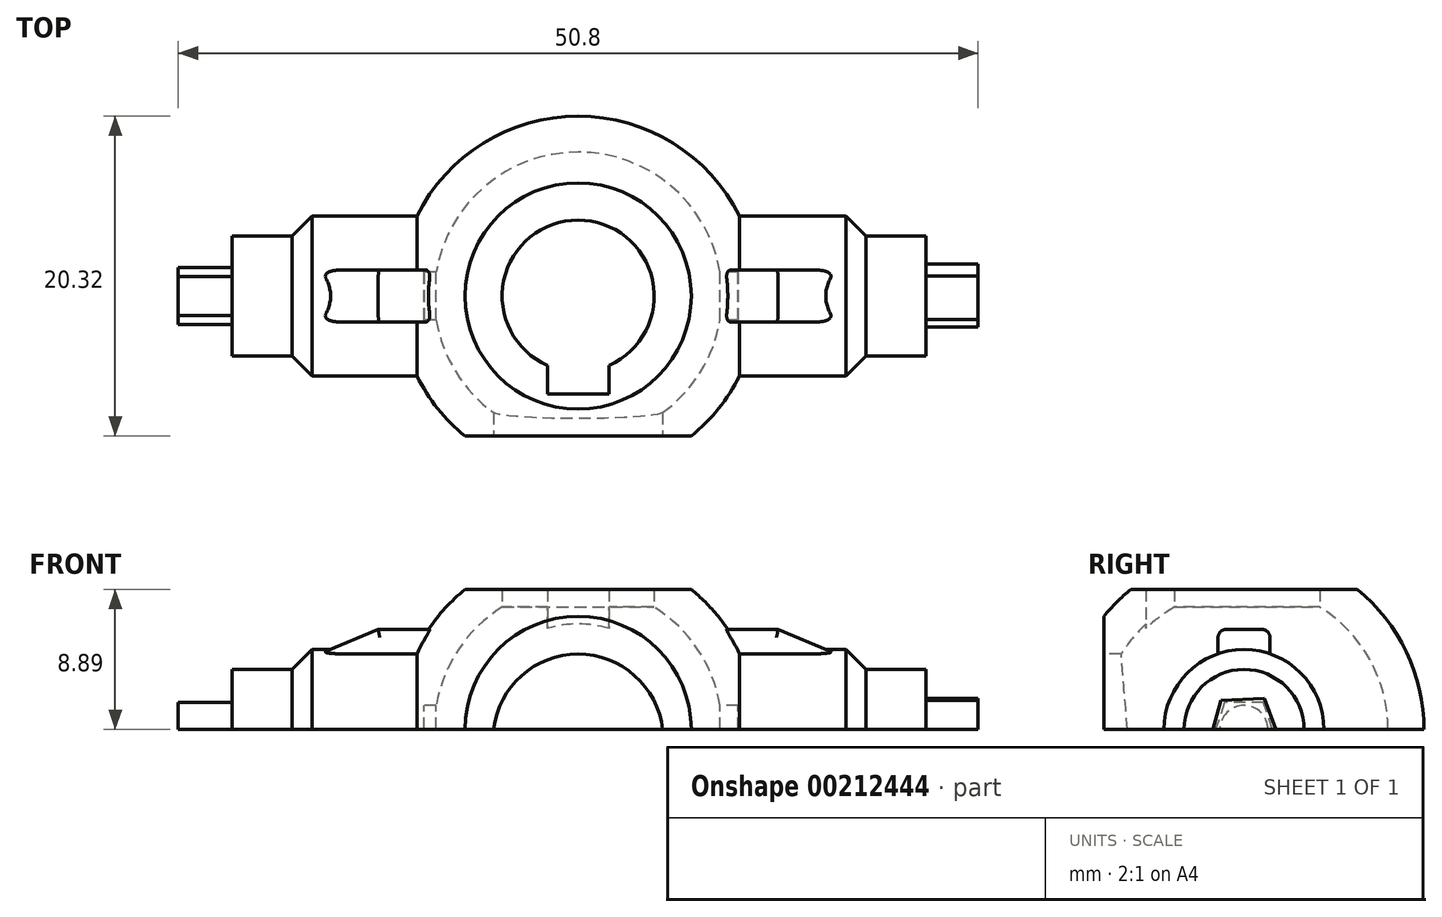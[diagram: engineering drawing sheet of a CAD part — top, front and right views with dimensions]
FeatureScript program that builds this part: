
annotation { "Feature Type Name" : "Feature", "Feature Type Description" : "" }
export const myFeature = defineFeature(function(context is Context, id is Id, definition is map)
    precondition{}
    {
        {
            var Q0;
            Q0=qCreatedBy(makeId("Top.planeOp"),FACE);
            var sketch = newSketch(context, id + "F0", { "sketchPlane" : qUnion([Q0])});
            skCircle(sketch, "E0", {"center": v(0, 0) * mm, "radius": 11.43 * mm});
            skSolve(sketch);
        }
        {
            var Q0;
            Q0=qCreatedBy(makeId("Right.planeOp"),FACE);
            var sketch = newSketch(context, id + "F1", { "sketchPlane" : qUnion([Q0])});
            skCircle(sketch, "E1", {"center": v(0, 0) * mm, "radius": 3.81 * mm});
            skSolve(sketch);
        }
        {
            var Q0;
            Q0=makeQuery(id+"F0.imprint","IMPRINT",FACE,{"disambiguationData":[TD([[makeQuery(id+"F0.imprint","IMPRINT",EDGE,{"derivedFrom":sQuery(id+"F0.wireOp",EDGE,"E0")}),1.0]])]});
            extrude(context, id + "F2", {"entities" : qUnion([Q0]), "depth" : 11.43 * mm});
        }
        {
            var Q0;
            Q0 = qSketchRegion(id + "F1", true);
            extrude(context, id + "F3", {"entities" : qUnion([Q0]), "operationType" : NewBodyOperationType.ADD, "depth" : 25.4 * mm, "hasSecondDirection" : true, "secondDirectionOppositeDirection" : true, "secondDirectionDepth" : 25.4 * mm});
        }
        {
            var Q0;
            Q0=makeQuery(id+"F2.opExtrude","CAP_EDGE",EDGE,{"disambiguationData":[OSD([sQuery(id+"F0.wireOp",EDGE,"E0")])],"isStart":false});
            fillet(context, id + "F4", {"entities" : qUnion([Q0]), "radius" : 11.43 * mm, "tangentPropagation" : true, "allowEdgeOverflow" : false});
        }
        {
            var Q0;
            Q0=makeQuery(id+"F2.opExtrude","CAP_FACE",FACE,{"disambiguationData":[OSD([sQuery(id+"F0.wireOp",EDGE,"E0")])],"isStart":true});
            shell(context, id + "F5", {"entities" : qUnion([Q0]), "thickness" : 2.3 * mm});
        }
        {
            var Q0;
            Q0=qCreatedBy(makeId("Top.planeOp"),FACE);
            var sketch = newSketch(context, id + "F6", { "sketchPlane" : qUnion([Q0])});
            skArc(sketch, "E2", {"start": v(1.96, -4.41) * mm, "mid": v(0, 4.83) * mm, "end": v(-1.94, -4.42) * mm});
            skLineSegment(sketch, "E3", {"start": v(0, -6.22) * mm, "end": v(-1.94, -6.22) * mm});
            skLineSegment(sketch, "E4", {"start": v(-1.94, -6.22) * mm, "end": v(-1.94, -4.42) * mm});
            skLineSegment(sketch, "E5", {"start": v(0, -6.22) * mm, "end": v(1.96, -6.22) * mm});
            skLineSegment(sketch, "E6", {"start": v(1.96, -6.22) * mm, "end": v(1.96, -4.41) * mm});
            skPoint(sketch, "E7.orphan", {"position": v(-1.94, 0) * mm});
            skPoint(sketch, "E8.orphan", {"position": v(1.96, 0) * mm});
            skSolve(sketch);
        }
        {
            var Q0;
            Q0 = qSketchRegion(id + "F6", true);
            extrude(context, id + "F7", {"entities" : qUnion([Q0]), "operationType" : NewBodyOperationType.REMOVE, "depth" : 25.4 * mm});
        }
        {
            var Q0;
            Q0=qCreatedBy(makeId("Top.planeOp"),FACE);
            var sketch = newSketch(context, id + "F8", { "sketchPlane" : qUnion([Q0])});
            skCircle(sketch, "E9", {"center": v(0, 0) * mm, "radius": 9.15 * mm});
            skSolve(sketch);
        }
        {
            var Q0;
            Q0 = qSketchRegion(id + "F8", true);
            extrude(context, id + "F9", {"entities" : qUnion([Q0]), "operationType" : NewBodyOperationType.REMOVE, "oppositeDirection" : true, "depth" : 25.4 * mm});
        }
        {
            var Q0;
            Q0=makeQuery(id+"F3.opExtrude","CAP_FACE",FACE,{"disambiguationData":[OSD([sQuery(id+"F1.wireOp",EDGE,"E1")])],"isStart":false});
            var sketch = newSketch(context, id + "F10", { "sketchPlane" : qUnion([Q0])});
            skCircle(sketch, "E10.cCircle", {"center": v(0, 0) * mm, "radius": 1.9 * mm, "construction": true});
            skLineSegment(sketch, "E10.0", {"start": v(1.28, 1.97) * mm, "end": v(2.27, -0.6) * mm});
            skLineSegment(sketch, "E10.1", {"start": v(2.27, -0.6) * mm, "end": v(0.12, -2.35) * mm});
            skLineSegment(sketch, "E10.2", {"start": v(0.12, -2.35) * mm, "end": v(-2.2, -0.84) * mm});
            skLineSegment(sketch, "E10.3", {"start": v(-2.2, -0.84) * mm, "end": v(-1.48, 1.83) * mm});
            skLineSegment(sketch, "E10.4", {"start": v(-1.48, 1.83) * mm, "end": v(1.28, 1.97) * mm});
            skPoint(sketch, "E10.0.midPoint", {"position": v(1.78, 0.68) * mm});
            skCircle(sketch, "E11", {"center": v(0, 0) * mm, "radius": 3.82 * mm});
            skSolve(sketch);
        }
        {
            var Q0;
            Q0 = qSketchRegion(id + "F10", true);
            extrude(context, id + "F11", {"entities" : qUnion([Q0]), "operationType" : NewBodyOperationType.REMOVE, "oppositeDirection" : true, "depth" : 3.3 * mm});
        }
        {
            var Q0;
            Q0=makeQuery(id+"F3.opExtrude","CAP_FACE",FACE,{"disambiguationData":[OSD([sQuery(id+"F1.wireOp",EDGE,"E1")])],"isStart":true});
            var sketch = newSketch(context, id + "F12", { "sketchPlane" : qUnion([Q0])});
            skCircle(sketch, "E12.cCircle", {"center": v(0, 0) * mm, "radius": 1.71 * mm, "construction": true});
            skLineSegment(sketch, "E12.0", {"start": v(-1.25, 1.71) * mm, "end": v(1.25, 1.71) * mm});
            skLineSegment(sketch, "E12.1", {"start": v(1.25, 1.71) * mm, "end": v(2.02, -0.65) * mm});
            skLineSegment(sketch, "E12.2", {"start": v(2.02, -0.65) * mm, "end": v(0, -2.12) * mm});
            skLineSegment(sketch, "E12.3", {"start": v(0, -2.12) * mm, "end": v(-2.02, -0.65) * mm});
            skLineSegment(sketch, "E12.4", {"start": v(-2.02, -0.65) * mm, "end": v(-1.25, 1.71) * mm});
            skPoint(sketch, "E12.0.midPoint", {"position": v(0, 1.71) * mm});
            skCircle(sketch, "E13", {"center": v(0, 0) * mm, "radius": 3.96 * mm});
            skSolve(sketch);
        }
        {
            var Q0;
            Q0 = qSketchRegion(id + "F12", true);
            extrude(context, id + "F13", {"entities" : qUnion([Q0]), "operationType" : NewBodyOperationType.REMOVE, "oppositeDirection" : true, "depth" : 3.43 * mm});
        }
        {
            var Q0;
            Q0=qCreatedBy(makeId("Right.planeOp"),FACE);
            var sketch = newSketch(context, id + "F14", { "sketchPlane" : qUnion([Q0])});
            skLineSegment(sketch, "E14", {"start": v(0, 0) * mm, "end": v(4.49, 0) * mm});
            skLineSegment(sketch, "E15", {"start": v(4.49, 0) * mm, "end": v(4.49, -5.61) * mm});
            skLineSegment(sketch, "E16", {"start": v(4.49, -5.61) * mm, "end": v(-4.03, -5.61) * mm});
            skLineSegment(sketch, "E17", {"start": v(-4.03, -5.61) * mm, "end": v(-4.03, 0) * mm});
            skLineSegment(sketch, "E18", {"start": v(-4.03, 0) * mm, "end": v(0, 0) * mm});
            skSolve(sketch);
        }
        {
            var Q0;
            Q0 = qSketchRegion(id + "F14", true);
            extrude(context, id + "F15", {"entities" : qUnion([Q0]), "operationType" : NewBodyOperationType.REMOVE, "endBound" : BoundingType.THROUGH_ALL, "oppositeDirection" : true, "depth" : 25.4 * mm, "hasSecondDirection" : true, "secondDirectionBound" : SecondDirectionBoundingType.THROUGH_ALL, "secondDirectionOppositeDirection" : false, "secondDirectionDepth" : 25.4 * mm});
        }
        {
            var Q0;
            {var subQ0=sQuery(id+"F1.wireOp",EDGE,"E1");Q0=makeQuery(id+"F5.opShell","OFFSET_FACE",FACE,{"disambiguationData":[OSD([subQ0]),TDD([makeQuery(id+"F3.opExtrude","CAP_FACE",FACE,{"disambiguationData":[OSD([subQ0])],"isStart":false})])]});}
            var sketch = newSketch(context, id + "F16", { "sketchPlane" : qUnion([Q0])});
            skLineSegment(sketch, "E19", {"start": v(-1.52, 0) * mm, "end": v(1.52, 0) * mm});
            skArc(sketch, "E20", {"start": v(1.52, 0) * mm, "mid": v(0, 1.53) * mm, "end": v(-1.52, 0) * mm});
            skSolve(sketch);
        }
        {
            var Q0;
            Q0 = qSketchRegion(id + "F16", true);
            extrude(context, id + "F17", {"entities" : qUnion([Q0]), "operationType" : NewBodyOperationType.ADD, "depth" : 7.62 * mm});
        }
        {
            var Q0;
            {var subQ0=sQuery(id+"F1.wireOp",EDGE,"E1");Q0=makeQuery(id+"F5.opShell","OFFSET_FACE",FACE,{"disambiguationData":[OSD([subQ0]),TDD([makeQuery(id+"F3.opExtrude","CAP_FACE",FACE,{"disambiguationData":[OSD([subQ0])],"isStart":true})])]});}
            var sketch = newSketch(context, id + "F18", { "sketchPlane" : qUnion([Q0])});
            skLineSegment(sketch, "E21", {"start": v(1.52, 0) * mm, "end": v(-1.52, 0) * mm});
            skArc(sketch, "E22", {"start": v(1.52, 0) * mm, "mid": v(0, 1.58) * mm, "end": v(-1.52, 0) * mm});
            skSolve(sketch);
        }
        {
            var Q0;
            Q0 = qSketchRegion(id + "F18", true);
            extrude(context, id + "F19", {"entities" : qUnion([Q0]), "operationType" : NewBodyOperationType.ADD, "depth" : 7.62 * mm});
        }
        {
            var Q0;
            Q0=qCreatedBy(makeId("Front.planeOp"),FACE);
            var sketch = newSketch(context, id + "F20", { "sketchPlane" : qUnion([Q0])});
            skLineSegment(sketch, "E23", {"start": v(7.45, 6.35) * mm, "end": v(12.7, 6.35) * mm});
            skLineSegment(sketch, "E24", {"start": v(-7.45, 6.35) * mm, "end": v(-12.7, 6.35) * mm});
            skArc(sketch, "E25", {"start": v(9.07, 3.68) * mm, "mid": v(8.37, 5.08) * mm, "end": v(7.45, 6.35) * mm});
            skLineSegment(sketch, "E26", {"start": v(12.7, 6.35) * mm, "end": v(19.05, 3.68) * mm});
            skLineSegment(sketch, "E27", {"start": v(-12.7, 6.35) * mm, "end": v(-19.05, 3.68) * mm});
            skArc(sketch, "E28.trimOffspring", {"start": v(-7.45, 6.35) * mm, "mid": v(-8.37, 5.08) * mm, "end": v(-9.07, 3.68) * mm});
            skLineSegment(sketch, "E29", {"start": v(-19.05, 2.55) * mm, "end": v(-9.07, 2.55) * mm});
            skLineSegment(sketch, "E30", {"start": v(19.05, 2.55) * mm, "end": v(19.05, 3.68) * mm});
            skLineSegment(sketch, "E31", {"start": v(-19.05, 3.68) * mm, "end": v(-19.05, 2.55) * mm});
            skLineSegment(sketch, "E32", {"start": v(-9.07, 3.68) * mm, "end": v(-9.07, 2.55) * mm});
            skLineSegment(sketch, "E33", {"start": v(9.07, 3.68) * mm, "end": v(9.07, 2.55) * mm});
            skLineSegment(sketch, "E34.trimOffspring", {"start": v(9.07, 2.55) * mm, "end": v(19.05, 2.55) * mm});
            skSolve(sketch);
        }
        {
            var Q0;
            Q0 = qSketchRegion(id + "F20", true);
            extrude(context, id + "F21", {"entities" : qUnion([Q0]), "operationType" : NewBodyOperationType.ADD, "depth" : 1.65 * mm, "hasSecondDirection" : true, "secondDirectionOppositeDirection" : true, "secondDirectionDepth" : 1.65 * mm});
        }
        {
            var Q0;
            Q0=makeQuery(id+"F21.opExtrude","CAP_EDGE",EDGE,{"disambiguationData":[OSD([sQuery(id+"F20.wireOp",EDGE,"E23")])],"isStart":false});
            var Q1;
            Q1=makeQuery(id+"F21.opExtrude","CAP_EDGE",EDGE,{"disambiguationData":[OSD([sQuery(id+"F20.wireOp",EDGE,"E23")])],"isStart":true});
            var Q2;
            Q2=makeQuery(id+"F21.opExtrude","CAP_EDGE",EDGE,{"disambiguationData":[OSD([sQuery(id+"F20.wireOp",EDGE,"E24")])],"isStart":false});
            var Q3;
            Q3=makeQuery(id+"F21.opExtrude","CAP_EDGE",EDGE,{"disambiguationData":[OSD([sQuery(id+"F20.wireOp",EDGE,"E24")])],"isStart":true});
            var Q4;
            Q4=makeQuery(id+"F21.opExtrude","CAP_EDGE",EDGE,{"disambiguationData":[OSD([sQuery(id+"F20.wireOp",EDGE,"E27")])],"isStart":true});
            var Q5;
            Q5=makeQuery(id+"F21.opExtrude","CAP_EDGE",EDGE,{"disambiguationData":[OSD([sQuery(id+"F20.wireOp",EDGE,"E27")])],"isStart":false});
            var Q6;
            Q6=makeQuery(id+"F21.opExtrude","CAP_EDGE",EDGE,{"disambiguationData":[OSD([sQuery(id+"F20.wireOp",EDGE,"E26")])],"isStart":false});
            var Q7;
            Q7=makeQuery(id+"F21.opExtrude","CAP_EDGE",EDGE,{"disambiguationData":[OSD([sQuery(id+"F20.wireOp",EDGE,"E26")])],"isStart":true});
            fillet(context, id + "F22", {"entities" : qUnion([Q0, Q1, Q2, Q3, Q4, Q5, Q6, Q7]), "radius" : 0.5 * mm, "tangentPropagation" : true, "allowEdgeOverflow" : false});
        }
        {
            var Q0;
            Q0=qCreatedBy(makeId("Right.planeOp"),FACE);
            var sketch = newSketch(context, id + "F23", { "sketchPlane" : qUnion([Q0])});
            skLineSegment(sketch, "E35", {"start": v(12.7, 8.9) * mm, "end": v(-12.7, 8.89) * mm});
            skLineSegment(sketch, "E36", {"start": v(12.7, 8.9) * mm, "end": v(12.7, 12.27) * mm});
            skLineSegment(sketch, "E37", {"start": v(12.7, 12.27) * mm, "end": v(-12.74, 12.27) * mm});
            skLineSegment(sketch, "E38", {"start": v(-12.74, 12.27) * mm, "end": v(-12.7, 8.89) * mm});
            skSolve(sketch);
        }
        {
            var Q0;
            Q0 = qSketchRegion(id + "F23", true);
            extrude(context, id + "F24", {"entities" : qUnion([Q0]), "operationType" : NewBodyOperationType.REMOVE, "oppositeDirection" : true, "depth" : 25.4 * mm, "hasSecondDirection" : true, "secondDirectionOppositeDirection" : false, "secondDirectionDepth" : 25.4 * mm});
        }
        {
            var Q0;
            Q0=qCreatedBy(makeId("Top.planeOp"),FACE);
            var sketch = newSketch(context, id + "F25", { "sketchPlane" : qUnion([Q0])});
            skLineSegment(sketch, "E39", {"start": v(-12.13, -8.9) * mm, "end": v(10.73, -8.9) * mm});
            skLineSegment(sketch, "E40", {"start": v(10.73, -8.9) * mm, "end": v(10.73, -14.7) * mm});
            skLineSegment(sketch, "E41", {"start": v(10.73, -14.7) * mm, "end": v(-12.13, -14.7) * mm});
            skLineSegment(sketch, "E42", {"start": v(-12.13, -14.7) * mm, "end": v(-12.13, -8.9) * mm});
            skSolve(sketch);
        }
        {
            var Q0;
            Q0 = qSketchRegion(id + "F25", true);
            extrude(context, id + "F26", {"entities" : qUnion([Q0]), "operationType" : NewBodyOperationType.REMOVE, "depth" : 25.4 * mm});
        }
        {
            var Q0;
            Q0=makeQuery(id+"F26.boolean.opBoolean","COPY",FACE,{"derivedFrom":makeQuery(id+"F26.opExtrude","SWEPT_FACE",FACE,{"disambiguationData":[OSD([sQuery(id+"F25.wireOp",EDGE,"E39")])]})});
            var sketch = newSketch(context, id + "F27", { "sketchPlane" : qUnion([Q0])});
            skPoint(sketch, "E43.center.orphan", {"position": v(0, -1.13) * mm});
            skCircle(sketch, "E44", {"center": v(0, -0.61) * mm, "radius": 5.4 * mm});
            skSolve(sketch);
        }
        {
            var Q0;
            Q0 = qSketchRegion(id + "F27", true);
            extrude(context, id + "F28", {"entities" : qUnion([Q0]), "operationType" : NewBodyOperationType.REMOVE, "oppositeDirection" : true, "depth" : 2.54 * mm});
        }
        {
            var Q0;
            Q0=makeQuery(id+"F11.boolean.opBoolean","COPY",FACE,{"derivedFrom":makeQuery(id+"F11.opExtrude","CAP_FACE",FACE,{"disambiguationData":[OSD([sQuery(id+"F10.wireOp",EDGE,"E10.0"),sQuery(id+"F10.wireOp",EDGE,"E10.1"),sQuery(id+"F10.wireOp",EDGE,"E10.2"),sQuery(id+"F10.wireOp",EDGE,"E10.3"),sQuery(id+"F10.wireOp",EDGE,"E10.4"),sQuery(id+"F10.wireOp",EDGE,"E11")])],"isStart":false})});
            var sketch = newSketch(context, id + "F29", { "sketchPlane" : qUnion([Q0])});
            skArc(sketch, "E45", {"start": v(5.08, -1.16) * mm, "mid": v(0, 3.92) * mm, "end": v(-5.08, -1.16) * mm});
            skLineSegment(sketch, "E46", {"start": v(-5.08, -1.16) * mm, "end": v(5.08, -1.16) * mm});
            skSolve(sketch);
        }
        {
            var Q0;
            Q0=makeQuery(id+"F29.imprint","IMPRINT",FACE,{"disambiguationData":[TD([[makeQuery(id+"F29.imprint","IMPRINT",EDGE,{"derivedFrom":sQuery(id+"F29.wireOp",EDGE,"E45")}),1.0]])]});
            cPlane(context, id + "F30", {"entities" : qUnion([Q0]), "cplaneType" : CPlaneType.OFFSET, "offset" : 2.54 * mm, "oppositeDirection" : true, "width" : 152.4 * mm, "height" : 152.4 * mm});
        }
        {
            var Q0;
            Q0=qCreatedBy(id+"F30.planeOp",FACE);
            var sketch = newSketch(context, id + "F31", { "sketchPlane" : qUnion([Q0])});
            skArc(sketch, "E47", {"start": v(5.08, 0) * mm, "mid": v(0, 5.08) * mm, "end": v(-5.08, 0) * mm});
            skLineSegment(sketch, "E48", {"start": v(-5.08, 0) * mm, "end": v(5.08, 0) * mm});
            skSolve(sketch);
        }
        {
            var Q0;
            Q0 = qSketchRegion(id + "F31", true);
            extrude(context, id + "F32", {"entities" : qUnion([Q0]), "operationType" : NewBodyOperationType.ADD, "oppositeDirection" : true, "depth" : 9.4 * mm});
        }
        {
            var Q0;
            Q0=makeQuery(id+"F13.boolean.opBoolean","COPY",FACE,{"derivedFrom":makeQuery(id+"F13.opExtrude","CAP_FACE",FACE,{"disambiguationData":[OSD([sQuery(id+"F12.wireOp",EDGE,"E12.0"),sQuery(id+"F12.wireOp",EDGE,"E12.1"),sQuery(id+"F12.wireOp",EDGE,"E12.2"),sQuery(id+"F12.wireOp",EDGE,"E12.3"),sQuery(id+"F12.wireOp",EDGE,"E12.4"),sQuery(id+"F12.wireOp",EDGE,"E13")])],"isStart":false})});
            cPlane(context, id + "F33", {"entities" : qUnion([Q0]), "cplaneType" : CPlaneType.OFFSET, "offset" : 2.54 * mm, "oppositeDirection" : true, "width" : 152.4 * mm, "height" : 152.4 * mm});
        }
        {
            var Q0;
            Q0=qCreatedBy(id+"F33.planeOp",FACE);
            var sketch = newSketch(context, id + "F34", { "sketchPlane" : qUnion([Q0])});
            skArc(sketch, "E49", {"start": v(5.08, 0) * mm, "mid": v(0, 5.08) * mm, "end": v(-5.08, 0) * mm});
            skLineSegment(sketch, "E50", {"start": v(-5.08, 0) * mm, "end": v(5.08, 0) * mm});
            skSolve(sketch);
        }
        {
            var Q0;
            Q0 = qSketchRegion(id + "F34", true);
            extrude(context, id + "F35", {"entities" : qUnion([Q0]), "operationType" : NewBodyOperationType.ADD, "oppositeDirection" : true, "depth" : 9.65 * mm});
        }
        {
            var Q0;
            Q0=makeQuery(id+"F35.opExtrude","CAP_EDGE",EDGE,{"disambiguationData":[OSD([sQuery(id+"F34.wireOp",EDGE,"E49")])],"isStart":true});
            var Q1;
            Q1=makeQuery(id+"F32.opExtrude","CAP_EDGE",EDGE,{"disambiguationData":[OSD([sQuery(id+"F31.wireOp",EDGE,"E47")])],"isStart":true});
            chamfer(context, id + "F36", {"entities" : qUnion([Q0, Q1]), "width" : 2.54 * mm, "tangentPropagation" : true});
        }
    });
